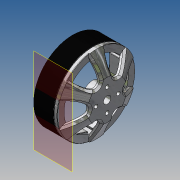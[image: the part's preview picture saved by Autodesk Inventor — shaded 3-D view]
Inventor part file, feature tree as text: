
AUTODESK INVENTOR PART (.ipt)
format: ipt  version: 2015 (Build 190159000, 159)  size: 617,984 bytes
history: native  units: mm
features: sketch x6, extrude x4, revolve x2, pattern_circular x2, fillet x2, chamfer x1, plane x1
ambient origin geometry x8: Origin, YZ Plane, XZ Plane, XY Plane, X Axis, Y Axis, Z Axis, Center Point
bodies: Solid1 (feature_tree)
feature tree (18):
  revolve  "Revolution1"  [1 undecoded]
  extrude  "Extrusion1"  Depth=20.9mm
  chamfer  "Chamfer1"  Distance=3.0mm
  pattern_circular  "Circular Pattern1"  [2 undecoded]
  plane  "Work Plane1"
  extrude  "Extrusion2"  TaperAngle=90.0deg  [1 undecoded]
  fillet  "Fillet1"  [1 undecoded]
  pattern_circular  "Circular Pattern2"  [2 undecoded]
  extrude  "Extrusion3"  Depth=2.0mm
  extrude  "Extrusion4"  Depth=2.0mm
  fillet  "Fillet2"  Radius=5.9mm
  revolve  "Revolution2"  Angle=45.0deg
  sketch  "Sketch1"  dims[d0=2.0mm d1=18.53mm]
  sketch  "Sketch3"  dims[d2=20.9mm d3=10.5mm]
  sketch  "Sketch4"  dims[d4=2.0mm]
  sketch  "Sketch5"  dims[d5=1.0mm]
  sketch  "Sketch6"  dims[d6=5.6mm]
  sketch  "Sketch7"  dims[d7=6.0mm d8=3.0mm d9=8.0mm d10=90.0deg d16=30.0deg d18=6.83mm d19=19.19mm d20=28.19mm d21=5.9mm d22=0.0mm d23=1.0mm d24=2.0mm d25=45.0deg d26=60.0mm d27=360.0deg d29=9.0mm d30=8.0mm d31=1.5mm d32=1.8mm d33=0.2mm d34=0.0mm d35=0.0mm d36=0.2mm d37=100.0mm d38=360.0deg d40=12.0mm d41=2.0mm d42=40.0mm d44=360.0deg d46=1.8mm d47=0.0mm d48=1.5mm d49=3.0mm d50=6.0mm d51=0.0mm d52=0.2mm d53=0.4mm d54=0.3mm d55=2.0mm d56=90.0deg]
note: 7 required parameter values undecoded (feature->parameter linkage not recoverable at this tier; creation-order binding heuristic only, values carry confidence <= 0.55)